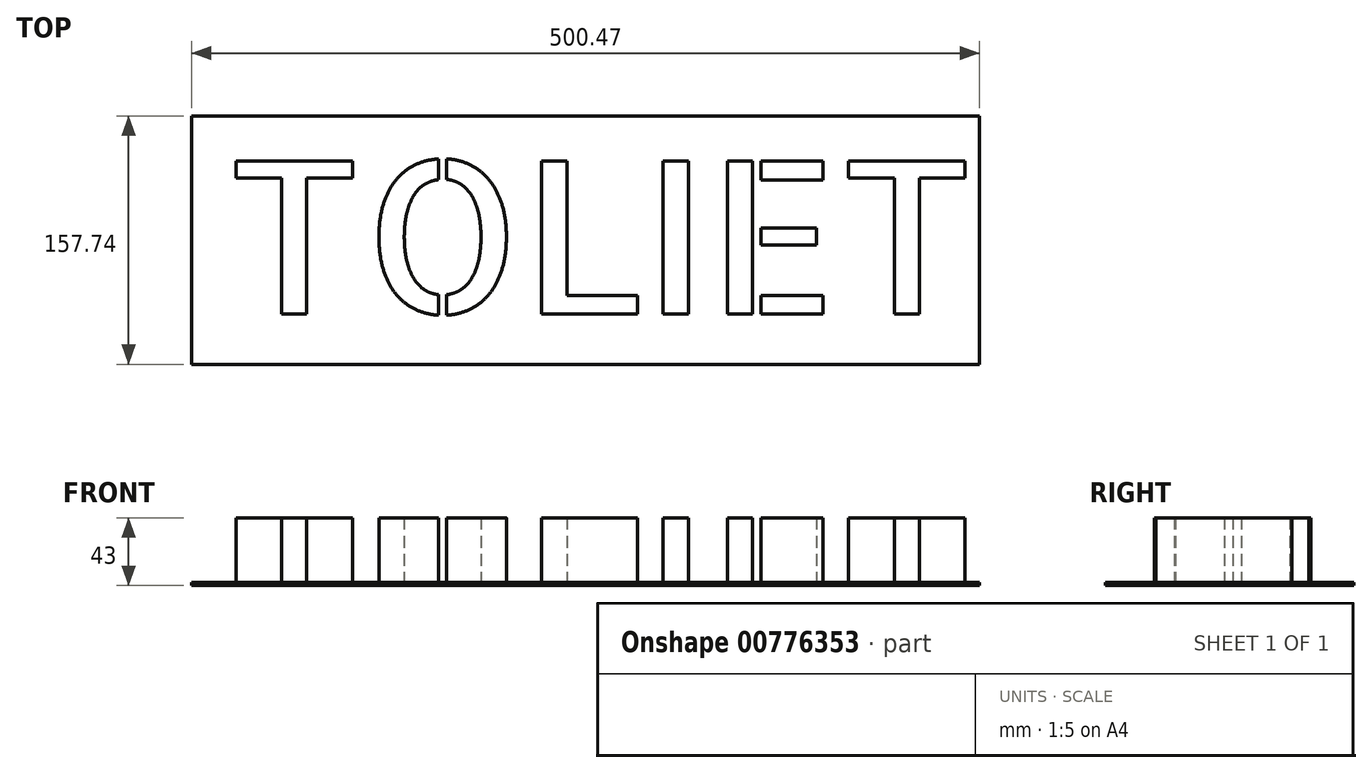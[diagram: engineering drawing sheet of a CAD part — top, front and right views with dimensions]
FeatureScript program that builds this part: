
annotation { "Feature Type Name" : "Feature", "Feature Type Description" : "" }
export const myFeature = defineFeature(function(context is Context, id is Id, definition is map)
    precondition{}
    {
        {
            var Q0;
            Q0=qCreatedBy(makeId("Top.planeOp"),FACE);
            var sketch = newSketch(context, id + "F0", { "sketchPlane" : qUnion([Q0])});
            skText(sketch, "E0", { "text": "TOLIET", "fontName": "AllertaStencil-Regular.ttf"});
            const initialGuessF0  = {"E0": [-0.14416, -0.03984, 1, 0, 0.09722]};
            skSetInitialGuess(sketch, initialGuessF0);
            skSolve(sketch);
        }
        {
            var Q0;
            Q0 = qSketchRegion(id + "F0", true);
            extrude(context, id + "F1", {"entities" : qUnion([Q0]), "depth" : 43 * mm, "offsetDistance" : 25 * mm});
        }
        {
            var Q0;
            Q0=qCreatedBy(makeId("Top.planeOp"),FACE);
            var sketch = newSketch(context, id + "F2", { "sketchPlane" : qUnion([Q0])});
            skLineSegment(sketch, "E1.bottom", {"start": v(-165.57, 86.05) * mm, "end": v(334.9, 86.05) * mm});
            skLineSegment(sketch, "E1.top", {"start": v(-165.57, -71.7) * mm, "end": v(334.9, -71.7) * mm});
            skLineSegment(sketch, "E1.left", {"start": v(-165.57, 86.05) * mm, "end": v(-165.57, -71.7) * mm});
            skLineSegment(sketch, "E1.right", {"start": v(334.9, 86.05) * mm, "end": v(334.9, -71.7) * mm});
            skSolve(sketch);
        }
        {
            var Q0;
            Q0 = qSketchRegion(id + "F2", true);
            extrude(context, id + "F3", {"entities" : qUnion([Q0]), "operationType" : NewBodyOperationType.ADD, "depth" : 2 * mm, "offsetDistance" : 25 * mm});
        }
    });
